# Revit family: YDILE
name_source: partatom
category: Luminaires
units: mm (PartAtom-declared; Revit-internal decimal feet)

## family parameters
Cote de connecteur circulaire = Utiliser le diamètre
Couper avec des vides une fois chargée = Oui
Hôte = Face
Numéro OmniClass = 23.80.70.11.17
Partagée = Oui
Point de calcul de pièce = Oui
Source d'éclairage = Oui
Titre OmniClass = Specialized Lighting by Location or Use
Type d'élément = Normal

## types (4) — shared parameters
Angle de l'inclinaison = 60.00°
Emettre la visibilité des formes dans le rendu = Non
Emettre à partir de la largeur du rectangle = 610 mm
Emettre à partir de la longueur du rectangle = 1219 mm
Fabricant = Résistex
Filtre de couleur = 16777215
Garantie = 5 ans
Gradation des changements de température de couleur de lampe = <Aucun>
IK = 08
IP = 20
Image du type = <Aucun>
Indice de charge = Eclairage
Largeur = 595 mm  [stored 1.9521 ft]
Longueur = 595 mm  [stored 1.9521 ft]
Matériau corps = Alu blanc
Matériau diffuseur = PC Transparent
Modèle = Ydile
Nombre pôles = 1
Tension = 230 V
URL = https://www.resistex-sa.com
Épaisseur = 18 mm  [stored 0.0590551 ft]
Épaisseur 2 = 2 mm  [stored 0.00656168 ft]
zero-valued in all types: Elévation par défaut

## per-type parameters (varying)
| type | Charge apparente | Commentaires relatifs à la puissance | Coût | Description | Fichier de distribution photométrique |
| 621470 | 22 VA | 21.5W | 75 $ | Encastré tertiaire équipé de platines LED SMD, efficacité lumineuse de 138.8lm/W | 621470.ies |
| 621471 | 22 VA | 21.5W | 75 $ | Encastré tertiaire équipé de platines LED SMD, efficacité lumineuse de 150.9lm/W | 621471.ies |
| 621472 | 37 VA | 35.1W | 147.5 $ | Encastré tertiaire équipé de platines LED SMD, efficacité lumineuse de 127lm/W | 621472.ies |
| 621473 | 37 VA | 35.6W | 147.5 $ | Encastré tertiaire équipé de platines LED SMD, efficacité lumineuse de 134.7lm/W | 621473.ies |

note: [stored X ft] marks values corroborated as IEEE doubles in the binary element streams (Revit-internal decimal feet)
